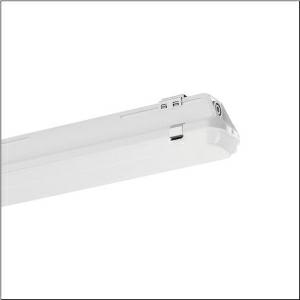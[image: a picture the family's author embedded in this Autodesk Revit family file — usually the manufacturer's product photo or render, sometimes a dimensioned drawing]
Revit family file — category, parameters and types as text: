
# Revit family: monsun_r__11_51fp10dp460l007_7819
name_source: partatom
category: Lighting Fixtures
units: mm (PartAtom-declared; Revit-internal decimal feet)

## family parameters
Cut with Voids When Loaded = No
Host = Face
Light Source = No
Part Type = Normal
Room Calculation Point = No
Round Connector Dimension = Use Diameter
Shared = No

## types (1)
- --- (1 x LED, 6050 lm, 31.5 W, 4000K)
    Apparent Load = 32 VA
    CIE Flux Codes = 47 77 93 94 100
    Color Rendering = 80
    Color Temperature = 4000K
    Default Elevation = 1800 mm
    Description = Monsun® 11, damp-proof luminaire, chain hanger, primary optical cover: enclosure, of PMMA, light emission: direct distribution, primary light characteristic: symmetric, installation type: suspended mounting, surface-mounted, horizontal mounting, vertical mounting, LED, rated luminous flux: 6.050lm, luminous efficacy: 192lm/W, light colour: 840, colour temperature: 4000K, control gear: DALI 2, with terminal, 5-pole, max. 2.5mm², through-wiring: 7x 2.5mm², mains connection: 220..240V, AC, 50/60Hz, rated input power: 32W, housing, of glass-fibre reinforced polyester, uncoated, bright grey, incl. chain hanger, length: 1.590mm, width: 90mm, height: 88mm, clip for enclosure, of stainless steel (V2A), ceiling mounting element, of stainless steel (V2A), chain hanger, of stainless steel (V2A), protection rating (complete): IP66, insulation class (complete): insulation class I (protective earthing), certification: CE, ENEC, VDE, UKCA, protection symbol: D, impact resistance: IK04, permissible operating ambient temperature: -25..+40°C, standard: EN 50419, EN 60598-2-1, corresponds to IFS (International Featured Standards) requirements for safety and quality in the food industry, for indoor or canopied outdoor use, no direct snow, no direct sun, no direct rain, LABS conformity tested according to VDMA 24364:2018-05, contact your sales advisor before using the luminaires in applications with unclear chemical exposure, large temperature fluctuations or condensation-forming humidity, packaging unit: 1 piece
    Height = 89 mm
    Lamp = 1 x LED
    Lamp Light Flux = 6050 lm
    Lamp Power = 31.5 W
    Lamp count = 1
    Length = 1590 mm
    Luminous efficacy = 192 lm/W
    Manufacturer = Siteco
    ModVariant = No
    Model = 51FP10DP460L007
    Mounting Place = Ceiling
    Mounting Type = Surface mounted
    Number of Poles = 1
    OnlyDefault = Yes
    Power Factor = 1
    Product Name = Monsun® 11
    Product group = damp-proof luminaire
    ProductGroupID = 300
    Protection Class = Protection class I
    Protection Degree = IP 66
    RLX_Detail_Level = 1
    RLX_Emergency_Light_Flux = 0 lm
    RLX_Emergency_Type = 0
    RLX_Emergency_Type_DB = No
    RlxData = <blob elided: 92049 chars, md5=4abe414b>
    Socket = socket
    Standby Power = 0 W
    System Light Flux = 6050 lm
    System Power = 32 W
    Type Comments = factory setting: luminous flux: 100 % | dim-lin: 254 | 219 mA
    Type Image = l_1349237.jpg
    URL = http://relux.com
    VarID = @adj_018052
    Voltage = 0 V
    Weight = 0.00 kg
    Width = 90 mm

## geometry (parser evidence)
native form markers: Blend x4, Sweep x12
no freeform markers — native parametric forms only
